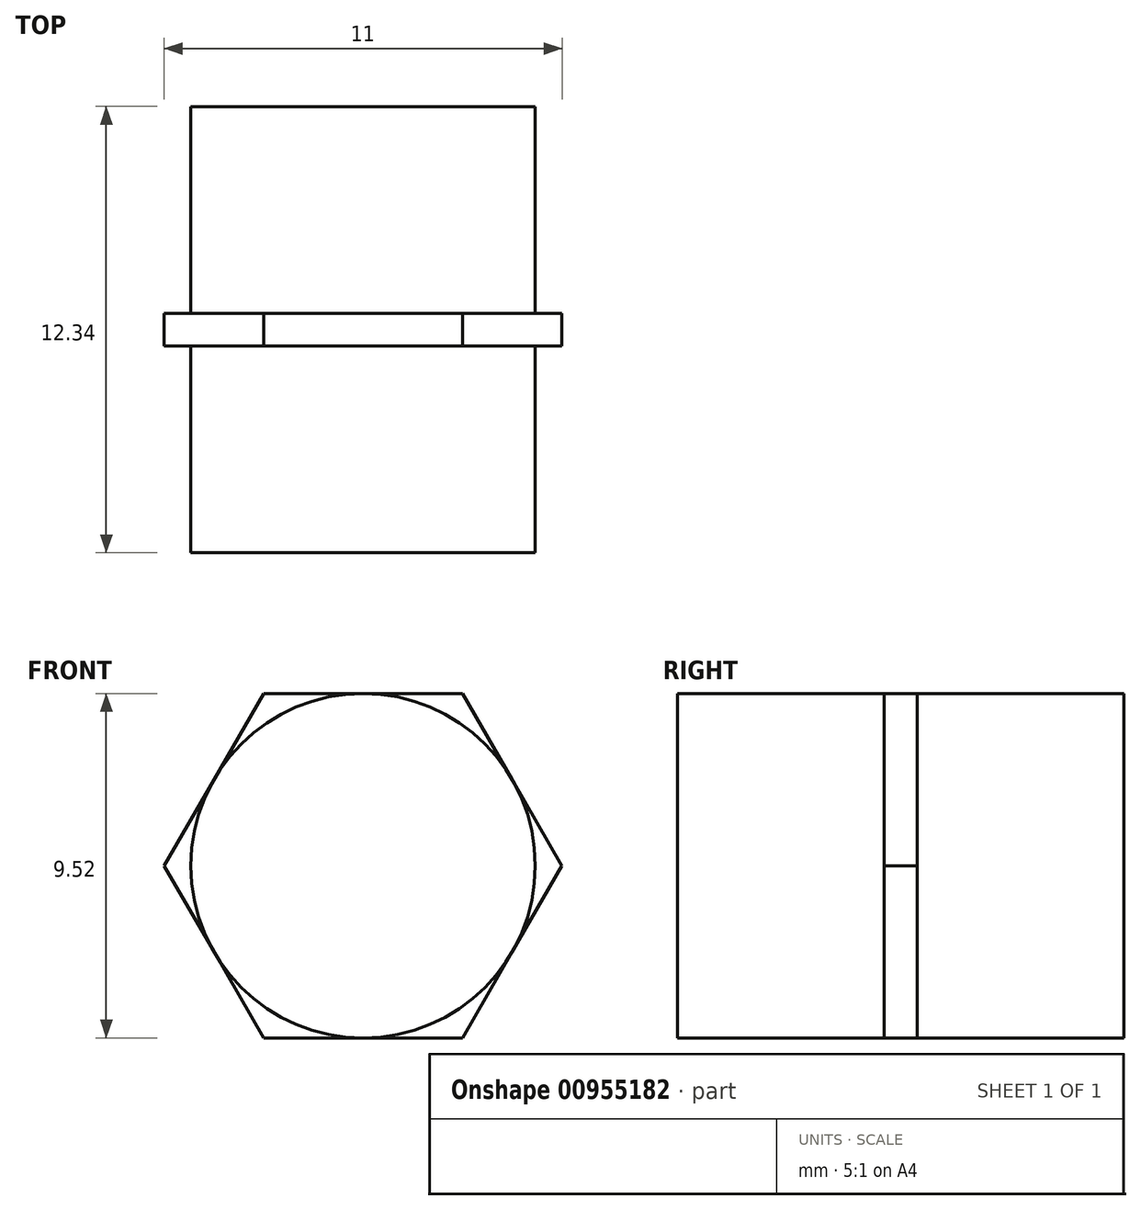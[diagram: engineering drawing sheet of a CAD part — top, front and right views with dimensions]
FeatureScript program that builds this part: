
annotation { "Feature Type Name" : "Feature", "Feature Type Description" : "" }
export const myFeature = defineFeature(function(context is Context, id is Id, definition is map)
    precondition{}
    {
        {
            var Q0;
            Q0=qCreatedBy(makeId("Front.planeOp"),FACE);
            var sketch = newSketch(context, id + "F0", { "sketchPlane" : qUnion([Q0])});
            skCircle(sketch, "E0.cCircle", {"center": v(0, 0) * mm, "radius": 4.76 * mm, "construction": true});
            skLineSegment(sketch, "E0.0", {"start": v(-2.75, 4.76) * mm, "end": v(2.75, 4.76) * mm});
            skLineSegment(sketch, "E0.1", {"start": v(2.75, 4.76) * mm, "end": v(5.5, 0) * mm});
            skLineSegment(sketch, "E0.2", {"start": v(5.5, 0) * mm, "end": v(2.75, -4.76) * mm});
            skLineSegment(sketch, "E0.3", {"start": v(2.75, -4.76) * mm, "end": v(-2.75, -4.76) * mm});
            skLineSegment(sketch, "E0.4", {"start": v(-2.75, -4.76) * mm, "end": v(-5.5, 0) * mm});
            skLineSegment(sketch, "E0.5", {"start": v(-5.5, 0) * mm, "end": v(-2.75, 4.76) * mm});
            skPoint(sketch, "E0.0.midPoint", {"position": v(0, 4.76) * mm});
            skSolve(sketch);
        }
        {
            var Q0;
            Q0=qSketchRegion(id+"F0",true);
            extrude(context, id + "F1", {"entities" : qUnion([Q0]), "depth" : (1.03 - (.125)) * mm, "offsetDistance" : 25.4 * mm});
        }
        {
            var Q0;
            Q0=makeQuery(id+"F1.opExtrude","CAP_FACE",FACE,{"disambiguationData":[OSD([sQuery(id+"F0.wireOp",EDGE,"E0.0"),sQuery(id+"F0.wireOp",EDGE,"E0.1"),sQuery(id+"F0.wireOp",EDGE,"E0.2"),sQuery(id+"F0.wireOp",EDGE,"E0.3"),sQuery(id+"F0.wireOp",EDGE,"E0.4"),sQuery(id+"F0.wireOp",EDGE,"E0.5")])],"isStart":false});
            var sketch = newSketch(context, id + "F2", { "sketchPlane" : qUnion([Q0])});
            skCircle(sketch, "E1", {"center": v(0, 0) * mm, "radius": 4.76 * mm});
            skSolve(sketch);
        }
        {
            var Q0;
            Q0=qSketchRegion(id+"F2",true);
            extrude(context, id + "F3", {"entities" : qUnion([Q0]), "operationType" : NewBodyOperationType.ADD, "depth" : 5.7 * mm, "offsetDistance" : 25.4 * mm});
        }
        {
            var Q0;
            Q0=makeQuery(id+"F1.opExtrude","CAP_FACE",FACE,{"disambiguationData":[OSD([sQuery(id+"F0.wireOp",EDGE,"E0.0"),sQuery(id+"F0.wireOp",EDGE,"E0.1"),sQuery(id+"F0.wireOp",EDGE,"E0.2"),sQuery(id+"F0.wireOp",EDGE,"E0.3"),sQuery(id+"F0.wireOp",EDGE,"E0.4"),sQuery(id+"F0.wireOp",EDGE,"E0.5")])],"isStart":true});
            var sketch = newSketch(context, id + "F4", { "sketchPlane" : qUnion([Q0])});
            skCircle(sketch, "E2", {"center": v(0, 0) * mm, "radius": 4.76 * mm});
            skSolve(sketch);
        }
        {
            var Q0;
            Q0=qSketchRegion(id+"F4",true);
            extrude(context, id + "F5", {"entities" : qUnion([Q0]), "operationType" : NewBodyOperationType.ADD, "depth" : 5.7 * mm, "offsetDistance" : 25.4 * mm});
        }
    });
